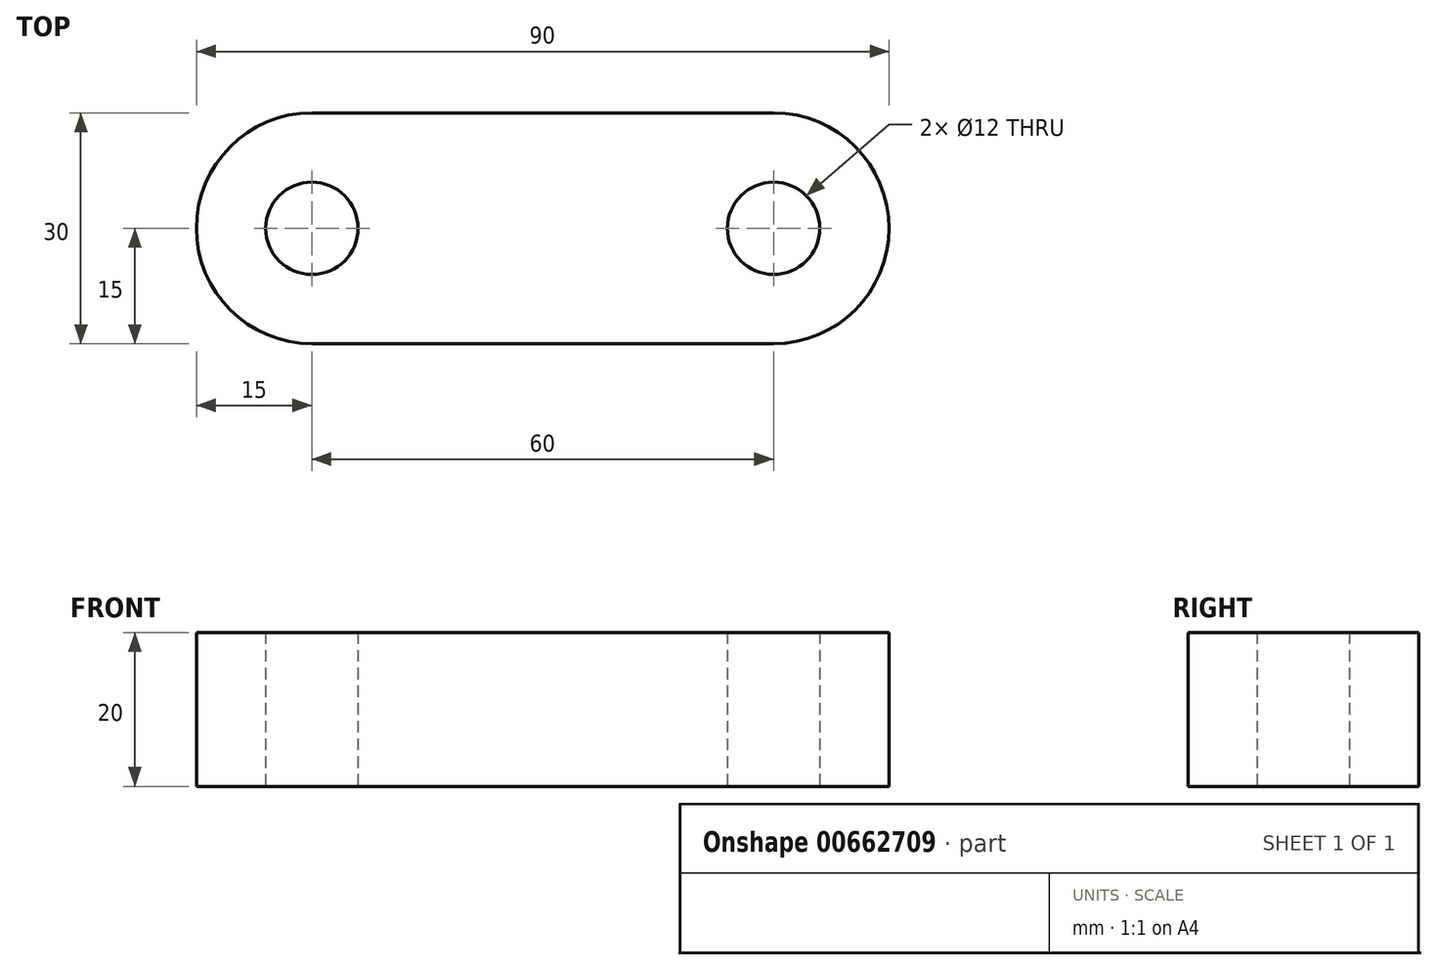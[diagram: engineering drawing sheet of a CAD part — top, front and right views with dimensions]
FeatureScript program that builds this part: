
annotation { "Feature Type Name" : "Feature", "Feature Type Description" : "" }
export const myFeature = defineFeature(function(context is Context, id is Id, definition is map)
    precondition{}
    {
        {
            var Q0;
            Q0=qCreatedBy(makeId("Top.planeOp"),FACE);
            var sketch = newSketch(context, id + "F0", { "sketchPlane" : qUnion([Q0])});
            skLineSegment(sketch, "E0", {"start": v(-30, 15) * mm, "end": v(30, 15) * mm});
            skLineSegment(sketch, "E1", {"start": v(-30, -15) * mm, "end": v(30, -15) * mm});
            skArc(sketch, "E2", {"start": v(30, -15) * mm, "mid": v(45, 0) * mm, "end": v(30, 15) * mm});
            skArc(sketch, "E3", {"start": v(-30, 15) * mm, "mid": v(-45, 0) * mm, "end": v(-30, -15) * mm});
            skCircle(sketch, "E4", {"center": v(-30, 0) * mm, "radius": 6 * mm});
            skCircle(sketch, "E5", {"center": v(30, 0) * mm, "radius": 6 * mm});
            skSolve(sketch);
        }
        {
            var Q0;
            Q0=makeQuery(id+"F0.imprint","IMPRINT",FACE,{"disambiguationData":[TD([[makeQuery(id+"F0.imprint","IMPRINT",EDGE,{"derivedFrom":sQuery(id+"F0.wireOp",EDGE,"E0")}),-1.0]])]});
            extrude(context, id + "F1", {"entities" : qUnion([Q0]), "depth" : 20 * mm, "offsetDistance" : 25 * mm});
        }
    });
